# Revit family: VIESSMANN - Vitocal 350-G Pro
name_source: partatom
category: Wyposażenie mechaniczne
revit_build: Autodesk Revit 2017 (Build: 20160720_1515(x64)
units: mm (PartAtom-declared; Revit-internal decimal feet)

## family parameters
Numer OmniClass = 23.75.10.21.17
Oparty na płaszczyźnie roboczej = Nie
Punkt obliczania pomieszczeń = Nie
Tnij formami wycięć po wczytaniu = Nie
Typ części = Normalny
Tytuł OmniClass = Water-Source Heat Pumps
Współdzielony = Nie
Wymiar okrągłego złącza = Użyj średnicy
Zawsze pionowo = Tak

## types (10) — shared parameters
Autor = www.archispace.pl
Czynnik chłodniczy = R134a
Częstotliwość = 50 Hz
Dopuszczalne ciśnienie robocze. Strona niskociśnieniowa = 1.6 MPa
Dopuszczalne ciśnienie robocze. Strona wysokociśnieniowa = 2.6 MPa
Długość strefy serwisowej od przodu = 800 mm  [stored 2.62467 ft]
Klasa efektywności energetycznej. Zastosowanie średniotemperaturowe (W55) = A+
Liczba biegunów = 3
Liczba obiegów chłodniczych = 1
Model = Solankowa pompa ciepła Vitocal 350-G PRO 80kW / Brine-water heat pump Vitocal 350-G PRO 80kW
Napięcie znamionowe = 400 V
Obieg pierwotny. Dop. ciśnienie robocze = 1.0 MPa
Obieg pierwotny. Ochrona przed zamarzaniem/temperatura początku krystalizacji (zalecany czynnik chłodzący Tyfocor) = -16 °C
Obieg pierwotny. Różnica temperatur = 3 °C
Obieg wtórny. Dop. ciśnienie robocze = 1.0 MPa
Obieg wtórny. Maks. temperatura na zasilaniu na wlocie z obiegu pierwotnego B -2°C = 73 °C
Obieg wtórny. Min. temperatura na zasilaniu zasobnika lodu = -10 °C
Obieg wtórny. Różnica temperatur = 5 °C
Opis = Pompy ciepła z napędem elektrycznym do ogrzewania i podgrzewu ciepłej wody użytkowej w jedno- lub dwusystemowych instalacjach grzewczych.
Podłączenie A odsunięcie = 389 mm  [stored 1.27625 ft]
Podłączenie A wysokość = 964 mm  [stored 3.16273 ft]
Podłączenie B odsunięcie = 389 mm  [stored 1.27625 ft]
Podłączenie B wysokość = 504 mm  [stored 1.65354 ft]
Podłączenie C odsunięcie = 106 mm  [stored 0.347769 ft]
Podłączenie C wysokość = 964 mm  [stored 3.16273 ft]
Podłączenie D odsunięcie = 106 mm  [stored 0.347769 ft]
Podłączenie D wysokość = 504 mm  [stored 1.65354 ft]
Podłączenie elektryczne odsunięcie = 697 mm
Podłączenie elektryczne wysokość = 1366 mm
Producent = Viessmann Sp. z o.o.
Rodzaj sprężarki = Tłok
Stopień ochrony = IP20
System rozruchowy = Moduł łagodnego rozruchu
URL = https://www.viessmann-projektant.pl
Viessmann Kolor 1 = Viessmann Kolor 1
Wewnętrzne zabezpieczenie pomp i zaworów (3/N/PE) = C40A
Zasilanie elektryczne (V/ph/Hz) = 3LNPE/400 V/50 Hz

## per-type parameters (varying)
- BW 352.B027: Całkowity maksymalny pobór mocy=31.0 kW; Całkowity prąd rozruchowy=74 A; Cos Phi sprężarki przy maks. mocy w B15/W35=0.63; Dane dotyczące mocy w trybie grzewczym. Zastosowanie niskotemperaturowe (W35). Efektywność energetyczna=147.00%; Dane dotyczące mocy w trybie grzewczym. Zastosowanie niskotemperaturowe (W35). Sezonowy stopień efektywności (SCOP)=3.87; Dane dotyczące mocy w trybie grzewczym. Zastosowanie średniotemperaturowe (W55). Efektywność energetyczna=112.00%; Dane dotyczące mocy w trybie grzewczym. Zastosowanie średniotemperaturowe (W55). Sezonowy stopień efektywności (SCOP)=3.01; Długość całkowita=1848 mm  [stored 6.06299 ft]; Ilość oleju=5.0 L; Klasa efektywności energetycznej. Zastosowanie niskotemperaturowe (W35)=A+; Liczba sprężarek=2; Maks. prąd roboczy=55 A; Maksymalne dopuszczalne zabezpieczenie zasilania przez inwestora=63 A; Masa całkowita (urządzenie podstawowe bez opcjonalnej obudowy)=555.00 kg; Natężenie znamionowe sprężarek (łącznie)=15 A; Obciążenie pozorne=49206 VA; Obieg pierwotny od strony parownika (Victaulic)=2½" (DN 65); Obieg pierwotny od strony zestawu przyłączy (kołnierz)=DN 65/PN 10; Obieg pierwotny. Minimalny przepływ objętościowy=4.8 m³/h; Obieg pierwotny. Opór przepływu przy minimalnym przepływie objętościowym=7.0 kPa; Obieg pierwotny. Opór przepływu przy znamionowym przepływie objętościowym (całkowita strata ciśnienia skraplacza z przyłączami)=12.0 kPa; Obieg pierwotny. Pojemność wymiennika ciepła (solanka)=4.4 L; Obieg pierwotny. Znamionowy przepływ objętościowy (wartość zalecana do projektowania)=6.4 m³/h; Obieg wtórny od strony skraplacza (Victaulic)=2½" (DN 65); Obieg wtórny od strony zestawu przyłączy (kołnierz)=DN 65/PN 10; Obieg wtórny. Minimalny przepływ objętościowy=3.5 m³/h; Obieg wtórny. Opór przepływu przy minimalnym przepływie objętościowym=8.0 kPa; Obieg wtórny. Opór przepływu przy znamionowym przepływie objętościowym (całkowita strata ciśnienia skraplacza z przyłączami)=15.0 kPa; Obieg wtórny. Pojemność wymiennika ciepła (woda)=3.7 L; Obieg wtórny. Znamionowy przepływ objętościowy (wartość zalecana do projektowania)=4.7 m³/h; Odsunięcie strefy serwisowej w szerokości=406 mm; Pobór mocy elektrycznej=6.4 kW; Poziom mocy akustycznej=53 dB(A); Prąd rozruchowy jednej sprężarki=32 A; Stopień efektywności ε (COP)=4.2; Szerokość całkowita=811 mm  [stored 2.66076 ft]; Typ=Vitocal 350-G Pro : BW 352.B027, BW 352.B034, BW 352.B056; Wewnętrzne zabezpieczenie na sprężarkę (3/N/PE)=gG25A; Wielkość napełnienia (wytyczna)=4.20 kg; Współczynnik mocy=0.63; Wydajność chłodnicza=20.8 kW; Wysokość całkowita=1450 mm  [stored 4.75722 ft]; Znamionowa moc grzewcza=27.2 kW; Średnica odejścia 1=65 mm  [stored 0.213255 ft]; Średnica odejścia 2=65 mm  [stored 0.213255 ft]
- BW 352.B034: Całkowity maksymalny pobór mocy=35.0 kW; Całkowity prąd rozruchowy=84 A; Cos Phi sprężarki przy maks. mocy w B15/W35=0.63; Dane dotyczące mocy w trybie grzewczym. Zastosowanie niskotemperaturowe (W35). Efektywność energetyczna=150.00%; Dane dotyczące mocy w trybie grzewczym. Zastosowanie niskotemperaturowe (W35). Sezonowy stopień efektywności (SCOP)=3.96; Dane dotyczące mocy w trybie grzewczym. Zastosowanie średniotemperaturowe (W55). Efektywność energetyczna=115.00%; Dane dotyczące mocy w trybie grzewczym. Zastosowanie średniotemperaturowe (W55). Sezonowy stopień efektywności (SCOP)=3.08; Długość całkowita=1848 mm  [stored 6.06299 ft]; Ilość oleju=6.6 L; Klasa efektywności energetycznej. Zastosowanie niskotemperaturowe (W35)=A++; Liczba sprężarek=2; Maks. prąd roboczy=61 A; Maksymalne dopuszczalne zabezpieczenie zasilania przez inwestora=63 A; Masa całkowita (urządzenie podstawowe bez opcjonalnej obudowy)=672.00 kg; Natężenie znamionowe sprężarek (łącznie)=18 A; Obciążenie pozorne=55556 VA; Obieg pierwotny od strony parownika (Victaulic)=2½" (DN 65); Obieg pierwotny od strony zestawu przyłączy (kołnierz)=DN 65/PN 10; Obieg pierwotny. Minimalny przepływ objętościowy=6.1 m³/h; Obieg pierwotny. Opór przepływu przy minimalnym przepływie objętościowym=7.0 kPa; Obieg pierwotny. Opór przepływu przy znamionowym przepływie objętościowym (całkowita strata ciśnienia skraplacza z przyłączami)=13.0 kPa; Obieg pierwotny. Pojemność wymiennika ciepła (solanka)=5.5 L; Obieg pierwotny. Znamionowy przepływ objętościowy (wartość zalecana do projektowania)=8.2 m³/h; Obieg wtórny od strony skraplacza (Victaulic)=2½" (DN 65); Obieg wtórny od strony zestawu przyłączy (kołnierz)=DN 65/PN 10; Obieg wtórny. Minimalny przepływ objętościowy=4.5 m³/h; Obieg wtórny. Opór przepływu przy minimalnym przepływie objętościowym=8.0 kPa; Obieg wtórny. Opór przepływu przy znamionowym przepływie objętościowym (całkowita strata ciśnienia skraplacza z przyłączami)=15.0 kPa; Obieg wtórny. Pojemność wymiennika ciepła (woda)=4.7 L; Obieg wtórny. Znamionowy przepływ objętościowy (wartość zalecana do projektowania)=5.9 m³/h; Odsunięcie strefy serwisowej w szerokości=406 mm; Pobór mocy elektrycznej=7.9 kW; Poziom mocy akustycznej=54 dB(A); Prąd rozruchowy jednej sprężarki=39 A; Stopień efektywności ε (COP)=4.4; Szerokość całkowita=811 mm  [stored 2.66076 ft]; Typ=Vitocal 350-G Pro : BW 352.B027, BW 352.B034, BW 352.B056; Wewnętrzne zabezpieczenie na sprężarkę (3/N/PE)=gG25A; Wielkość napełnienia (wytyczna)=5.20 kg; Współczynnik mocy=0.63; Wydajność chłodnicza=26.4 kW; Wysokość całkowita=1450 mm  [stored 4.75722 ft]; Znamionowa moc grzewcza=34.3 kW; Średnica odejścia 1=65 mm  [stored 0.213255 ft]; Średnica odejścia 2=65 mm  [stored 0.213255 ft]
- BW 352.B056: Całkowity maksymalny pobór mocy=47.0 kW; Całkowity prąd rozruchowy=120 A; Cos Phi sprężarki przy maks. mocy w B15/W35=0.71; Dane dotyczące mocy w trybie grzewczym. Zastosowanie niskotemperaturowe (W35). Efektywność energetyczna=153.00%; Dane dotyczące mocy w trybie grzewczym. Zastosowanie niskotemperaturowe (W35). Sezonowy stopień efektywności (SCOP)=4.03; Dane dotyczące mocy w trybie grzewczym. Zastosowanie średniotemperaturowe (W55). Efektywność energetyczna=117.00%; Dane dotyczące mocy w trybie grzewczym. Zastosowanie średniotemperaturowe (W55). Sezonowy stopień efektywności (SCOP)=3.12; Długość całkowita=1848 mm  [stored 6.06299 ft]; Ilość oleju=6.6 L; Klasa efektywności energetycznej. Zastosowanie niskotemperaturowe (W35)=A++; Liczba sprężarek=2; Maks. prąd roboczy=82 A; Maksymalne dopuszczalne zabezpieczenie zasilania przez inwestora=100 A; Masa całkowita (urządzenie podstawowe bez opcjonalnej obudowy)=723.00 kg; Natężenie znamionowe sprężarek (łącznie)=29 A; Obciążenie pozorne=66197 VA; Obieg pierwotny od strony parownika (Victaulic)=2½" (DN 65); Obieg pierwotny od strony zestawu przyłączy (kołnierz)=DN 65/PN 10; Obieg pierwotny. Minimalny przepływ objętościowy=10.1 m³/h; Obieg pierwotny. Opór przepływu przy minimalnym przepływie objętościowym=8.0 kPa; Obieg pierwotny. Opór przepływu przy znamionowym przepływie objętościowym (całkowita strata ciśnienia skraplacza z przyłączami)=14.0 kPa; Obieg pierwotny. Pojemność wymiennika ciepła (solanka)=9.4 L; Obieg pierwotny. Znamionowy przepływ objętościowy (wartość zalecana do projektowania)=13.4 m³/h; Obieg wtórny od strony skraplacza (Victaulic)=2½" (DN 65); Obieg wtórny od strony zestawu przyłączy (kołnierz)=DN 65/PN 10; Obieg wtórny. Minimalny przepływ objętościowy=7.3 m³/h; Obieg wtórny. Opór przepływu przy minimalnym przepływie objętościowym=9.0 kPa; Obieg wtórny. Opór przepływu przy znamionowym przepływie objętościowym (całkowita strata ciśnienia skraplacza z przyłączami)=16.0 kPa; Obieg wtórny. Pojemność wymiennika ciepła (woda)=7.4 L; Obieg wtórny. Znamionowy przepływ objętościowy (wartość zalecana do projektowania)=9.7 m³/h; Odsunięcie strefy serwisowej w szerokości=406 mm; Pobór mocy elektrycznej=12.8 kW; Poziom mocy akustycznej=58 dB(A); Prąd rozruchowy jednej sprężarki=65 A; Stopień efektywności ε (COP)=4.4; Szerokość całkowita=811 mm  [stored 2.66076 ft]; Typ=Vitocal 350-G Pro : BW 352.B027, BW 352.B034, BW 352.B056; Wewnętrzne zabezpieczenie na sprężarkę (3/N/PE)=gG40A; Wielkość napełnienia (wytyczna)=5.20 kg; Współczynnik mocy=0.71; Wydajność chłodnicza=43.4 kW; Wysokość całkowita=1450 mm  [stored 4.75722 ft]; Znamionowa moc grzewcza=56.1 kW; Średnica odejścia 1=65 mm  [stored 0.213255 ft]; Średnica odejścia 2=65 mm  [stored 0.213255 ft]
- BW 352.B076: Całkowity maksymalny pobór mocy=56.0 kW; Całkowity prąd rozruchowy=149 A; Cos Phi sprężarki przy maks. mocy w B15/W35=0.71; Dane dotyczące mocy w trybie grzewczym. Zastosowanie niskotemperaturowe (W35). Efektywność energetyczna=154.00%; Dane dotyczące mocy w trybie grzewczym. Zastosowanie niskotemperaturowe (W35). Sezonowy stopień efektywności (SCOP)=4.04; Dane dotyczące mocy w trybie grzewczym. Zastosowanie średniotemperaturowe (W55). Efektywność energetyczna=118.00%; Dane dotyczące mocy w trybie grzewczym. Zastosowanie średniotemperaturowe (W55). Sezonowy stopień efektywności (SCOP)=3.14; Długość całkowita=2153 mm  [stored 7.06365 ft]; Ilość oleju=9.0 L; Klasa efektywności energetycznej. Zastosowanie niskotemperaturowe (W35)=A++; Liczba sprężarek=2; Maks. prąd roboczy=98 A; Maksymalne dopuszczalne zabezpieczenie zasilania przez inwestora=100 A; Masa całkowita (urządzenie podstawowe bez opcjonalnej obudowy)=963.00 kg; Natężenie znamionowe sprężarek (łącznie)=36 A; Obciążenie pozorne=78873 VA; Obieg pierwotny od strony parownika (Victaulic)=2½" (DN 65); Obieg pierwotny od strony zestawu przyłączy (kołnierz)=DN 65/PN 10; Obieg pierwotny. Minimalny przepływ objętościowy=13.6 m³/h; Obieg pierwotny. Opór przepływu przy minimalnym przepływie objętościowym=9.0 kPa; Obieg pierwotny. Opór przepływu przy znamionowym przepływie objętościowym (całkowita strata ciśnienia skraplacza z przyłączami)=17.0 kPa; Obieg pierwotny. Pojemność wymiennika ciepła (solanka)=12.9 L; Obieg pierwotny. Znamionowy przepływ objętościowy (wartość zalecana do projektowania)=18.2 m³/h; Obieg wtórny od strony skraplacza (Victaulic)=2½" (DN 65); Obieg wtórny od strony zestawu przyłączy (kołnierz)=DN 65/PN 10; Obieg wtórny. Minimalny przepływ objętościowy=9.9 m³/h; Obieg wtórny. Opór przepływu przy minimalnym przepływie objętościowym=9.0 kPa; Obieg wtórny. Opór przepływu przy znamionowym przepływie objętościowym (całkowita strata ciśnienia skraplacza z przyłączami)=16.0 kPa; Obieg wtórny. Pojemność wymiennika ciepła (woda)=10.2 L; Obieg wtórny. Znamionowy przepływ objętościowy (wartość zalecana do projektowania)=13.2 m³/h; Odsunięcie strefy serwisowej w szerokości=456 mm; Pobór mocy elektrycznej=17.3 kW; Poziom mocy akustycznej=60 dB(A); Prąd rozruchowy jednej sprężarki=86 A; Stopień efektywności ε (COP)=4.4; Szerokość całkowita=911 mm  [stored 2.98885 ft]; Typ=Vitocal 350-G Pro : BW 352.B076, BW 352.B097, BW 352.B114; Wewnętrzne zabezpieczenie na sprężarkę (3/N/PE)=gG63A; Wielkość napełnienia (wytyczna)=7.50 kg; Współczynnik mocy=0.71; Wydajność chłodnicza=58.8 kW; Wysokość całkowita=1650 mm  [stored 5.41339 ft]; Znamionowa moc grzewcza=76.0 kW; Średnica odejścia 1=65 mm  [stored 0.213255 ft]; Średnica odejścia 2=65 mm  [stored 0.213255 ft]
- BW 352.B097: Całkowity maksymalny pobór mocy=69.0 kW; Całkowity prąd rozruchowy=179 A; Cos Phi sprężarki przy maks. mocy w B15/W35=0.66; Dane dotyczące mocy w trybie grzewczym. Zastosowanie niskotemperaturowe (W35). Efektywność energetyczna=154.00%; Dane dotyczące mocy w trybie grzewczym. Zastosowanie niskotemperaturowe (W35). Sezonowy stopień efektywności (SCOP)=4.06; Dane dotyczące mocy w trybie grzewczym. Zastosowanie średniotemperaturowe (W55). Efektywność energetyczna=118.00%; Dane dotyczące mocy w trybie grzewczym. Zastosowanie średniotemperaturowe (W55). Sezonowy stopień efektywności (SCOP)=3.15; Długość całkowita=2153 mm  [stored 7.06365 ft]; Ilość oleju=10.5 L; Klasa efektywności energetycznej. Zastosowanie niskotemperaturowe (W35)=A++; Liczba sprężarek=2; Maks. prąd roboczy=122 A; Maksymalne dopuszczalne zabezpieczenie zasilania przez inwestora=125 A; Masa całkowita (urządzenie podstawowe bez opcjonalnej obudowy)=1065.00 kg; Natężenie znamionowe sprężarek (łącznie)=54 A; Obciążenie pozorne=104545 VA; Obieg pierwotny od strony parownika (Victaulic)=2½" (DN 65); Obieg pierwotny od strony zestawu przyłączy (kołnierz)=DN 65/PN 10; Obieg pierwotny. Minimalny przepływ objętościowy=17.3 m³/h; Obieg pierwotny. Opór przepływu przy minimalnym przepływie objętościowym=11.0 kPa; Obieg pierwotny. Opór przepływu przy znamionowym przepływie objętościowym (całkowita strata ciśnienia skraplacza z przyłączami)=19.0 kPa; Obieg pierwotny. Pojemność wymiennika ciepła (solanka)=17.7 L; Obieg pierwotny. Znamionowy przepływ objętościowy (wartość zalecana do projektowania)=23.0 m³/h; Obieg wtórny od strony skraplacza (Victaulic)=2½" (DN 65); Obieg wtórny od strony zestawu przyłączy (kołnierz)=DN 65/PN 10; Obieg wtórny. Minimalny przepływ objętościowy=12.6 m³/h; Obieg wtórny. Opór przepływu przy minimalnym przepływie objętościowym=10.0 kPa; Obieg wtórny. Opór przepływu przy znamionowym przepływie objętościowym (całkowita strata ciśnienia skraplacza z przyłączami)=18.0 kPa; Obieg wtórny. Pojemność wymiennika ciepła (woda)=12.7 L; Obieg wtórny. Znamionowy przepływ objętościowy (wartość zalecana do projektowania)=16.8 m³/h; Odsunięcie strefy serwisowej w szerokości=456 mm; Pobór mocy elektrycznej=21.9 kW; Poziom mocy akustycznej=63 dB(A); Prąd rozruchowy jednej sprężarki=104 A; Stopień efektywności ε (COP)=4.4; Szerokość całkowita=911 mm  [stored 2.98885 ft]; Typ=Vitocal 350-G Pro : BW 352.B076, BW 352.B097, BW 352.B114; Wewnętrzne zabezpieczenie na sprężarkę (3/N/PE)=gG63A; Wielkość napełnienia (wytyczna)=10.00 kg; Współczynnik mocy=0.66; Wydajność chłodnicza=74.6 kW; Wysokość całkowita=1650 mm  [stored 5.41339 ft]; Znamionowa moc grzewcza=96.9 kW; Średnica odejścia 1=65 mm  [stored 0.213255 ft]; Średnica odejścia 2=65 mm  [stored 0.213255 ft]
- BW 352.B114: Całkowity maksymalny pobór mocy=78.0 kW; Całkowity prąd rozruchowy=208 A; Cos Phi sprężarki przy maks. mocy w B15/W35=0.7; Dane dotyczące mocy w trybie grzewczym. Zastosowanie niskotemperaturowe (W35). Efektywność energetyczna=153.00%; Dane dotyczące mocy w trybie grzewczym. Zastosowanie niskotemperaturowe (W35). Sezonowy stopień efektywności (SCOP)=4.03; Dane dotyczące mocy w trybie grzewczym. Zastosowanie średniotemperaturowe (W55). Efektywność energetyczna=117.00%; Dane dotyczące mocy w trybie grzewczym. Zastosowanie średniotemperaturowe (W55). Sezonowy stopień efektywności (SCOP)=3.14; Długość całkowita=2153 mm  [stored 7.06365 ft]; Ilość oleju=10.5 L; Klasa efektywności energetycznej. Zastosowanie niskotemperaturowe (W35)=A++; Liczba sprężarek=2; Maks. prąd roboczy=137 A; Maksymalne dopuszczalne zabezpieczenie zasilania przez inwestora=160 A; Masa całkowita (urządzenie podstawowe bez opcjonalnej obudowy)=1113.00 kg; Natężenie znamionowe sprężarek (łącznie)=57 A; Obciążenie pozorne=111429 VA; Obieg pierwotny od strony parownika (Victaulic)=3" (DN 80); Obieg pierwotny od strony zestawu przyłączy (kołnierz)=DN 80/PN 10; Obieg pierwotny. Minimalny przepływ objętościowy=20.5 m³/h; Obieg pierwotny. Opór przepływu przy minimalnym przepływie objętościowym=13.0 kPa; Obieg pierwotny. Opór przepływu przy znamionowym przepływie objętościowym (całkowita strata ciśnienia skraplacza z przyłączami)=23.0 kPa; Obieg pierwotny. Pojemność wymiennika ciepła (solanka)=21.9 L; Obieg pierwotny. Znamionowy przepływ objętościowy (wartość zalecana do projektowania)=27.3 m³/h; Obieg wtórny od strony skraplacza (Victaulic)=3" (DN 80); Obieg wtórny od strony zestawu przyłączy (kołnierz)=DN 80/PN 10; Obieg wtórny. Minimalny przepływ objętościowy=14.8 m³/h; Obieg wtórny. Opór przepływu przy minimalnym przepływie objętościowym=11.0 kPa; Obieg wtórny. Opór przepływu przy znamionowym przepływie objętościowym (całkowita strata ciśnienia skraplacza z przyłączami)=20.0 kPa; Obieg wtórny. Pojemność wymiennika ciepła (woda)=14.9 L; Obieg wtórny. Znamionowy przepływ objętościowy (wartość zalecana do projektowania)=19.8 m³/h; Odsunięcie strefy serwisowej w szerokości=456 mm; Pobór mocy elektrycznej=25.9 kW; Poziom mocy akustycznej=65 dB(A); Prąd rozruchowy jednej sprężarki=126 A; Stopień efektywności ε (COP)=4.4; Szerokość całkowita=911 mm  [stored 2.98885 ft]; Typ=Vitocal 350-G Pro : BW 352.B076, BW 352.B097, BW 352.B114; Wewnętrzne zabezpieczenie na sprężarkę (3/N/PE)=gG63A; Wielkość napełnienia (wytyczna)=12.00 kg; Współczynnik mocy=0.7; Wydajność chłodnicza=88.4 kW; Wysokość całkowita=1650 mm  [stored 5.41339 ft]; Znamionowa moc grzewcza=114.2 kW; Średnica odejścia 1=80 mm  [stored 0.262467 ft]; Średnica odejścia 2=80 mm  [stored 0.262467 ft]
- BW 352.B132: Całkowity maksymalny pobór mocy=89.0 kW; Całkowity prąd rozruchowy=237 A; Cos Phi sprężarki przy maks. mocy w B15/W35=0.66; Dane dotyczące mocy w trybie grzewczym. Zastosowanie niskotemperaturowe (W35). Efektywność energetyczna=150.00%; Dane dotyczące mocy w trybie grzewczym. Zastosowanie niskotemperaturowe (W35). Sezonowy stopień efektywności (SCOP)=3.95; Dane dotyczące mocy w trybie grzewczym. Zastosowanie średniotemperaturowe (W55). Efektywność energetyczna=116.00%; Dane dotyczące mocy w trybie grzewczym. Zastosowanie średniotemperaturowe (W55). Sezonowy stopień efektywności (SCOP)=3.1; Długość całkowita=2153 mm  [stored 7.06365 ft]; Ilość oleju=10.5 L; Klasa efektywności energetycznej. Zastosowanie niskotemperaturowe (W35)=A+; Liczba sprężarek=2; Maks. prąd roboczy=156 A; Maksymalne dopuszczalne zabezpieczenie zasilania przez inwestora=160 A; Masa całkowita (urządzenie podstawowe bez opcjonalnej obudowy)=1209.00 kg; Natężenie znamionowe sprężarek (łącznie)=73 A; Obciążenie pozorne=134848 VA; Obieg pierwotny od strony parownika (Victaulic)=3" (DN 80); Obieg pierwotny od strony zestawu przyłączy (kołnierz)=DN 80/PN 10; Obieg pierwotny. Minimalny przepływ objętościowy=23.5 m³/h; Obieg pierwotny. Opór przepływu przy minimalnym przepływie objętościowym=18.0 kPa; Obieg pierwotny. Opór przepływu przy znamionowym przepływie objętościowym (całkowita strata ciśnienia skraplacza z przyłączami)=32.0 kPa; Obieg pierwotny. Pojemność wymiennika ciepła (solanka)=33.6 L; Obieg pierwotny. Znamionowy przepływ objętościowy (wartość zalecana do projektowania)=31.3 m³/h; Obieg wtórny od strony skraplacza (Victaulic)=3" (DN 80); Obieg wtórny od strony zestawu przyłączy (kołnierz)=DN 80/PN 10; Obieg wtórny. Minimalny przepływ objętościowy=17.1 m³/h; Obieg wtórny. Opór przepływu przy minimalnym przepływie objętościowym=13.0 kPa; Obieg wtórny. Opór przepływu przy znamionowym przepływie objętościowym (całkowita strata ciśnienia skraplacza z przyłączami)=23.0 kPa; Obieg wtórny. Pojemność wymiennika ciepła (woda)=16.7 L; Obieg wtórny. Znamionowy przepływ objętościowy (wartość zalecana do projektowania)=22.9 m³/h; Odsunięcie strefy serwisowej w szerokości=456 mm; Pobór mocy elektrycznej=30.4 kW; Poziom mocy akustycznej=65 dB(A); Prąd rozruchowy jednej sprężarki=144 A; Stopień efektywności ε (COP)=4.3; Szerokość całkowita=911 mm  [stored 2.98885 ft]; Typ=Vitocal 350-G Pro : BW 352.B132, BW 352.B156; Wewnętrzne zabezpieczenie na sprężarkę (3/N/PE)=gG80A; Wielkość napełnienia (wytyczna)=14.00 kg; Współczynnik mocy=0.66; Wydajność chłodnicza=101.5 kW; Wysokość całkowita=1650 mm  [stored 5.41339 ft]; Znamionowa moc grzewcza=131.9 kW; Średnica odejścia 1=80 mm  [stored 0.262467 ft]; Średnica odejścia 2=80 mm  [stored 0.262467 ft]
- BW 352.B156: Całkowity maksymalny pobór mocy=97.0 kW; Całkowity prąd rozruchowy=245 A; Cos Phi sprężarki przy maks. mocy w B15/W35=0.57; Dane dotyczące mocy w trybie grzewczym. Zastosowanie niskotemperaturowe (W35). Efektywność energetyczna=150.00%; Dane dotyczące mocy w trybie grzewczym. Zastosowanie niskotemperaturowe (W35). Sezonowy stopień efektywności (SCOP)=3.95; Dane dotyczące mocy w trybie grzewczym. Zastosowanie średniotemperaturowe (W55). Efektywność energetyczna=116.00%; Dane dotyczące mocy w trybie grzewczym. Zastosowanie średniotemperaturowe (W55). Sezonowy stopień efektywności (SCOP)=3.1; Długość całkowita=2153 mm  [stored 7.06365 ft]; Ilość oleju=10.5 L; Klasa efektywności energetycznej. Zastosowanie niskotemperaturowe (W35)=A+; Liczba sprężarek=2; Maks. prąd roboczy=187 A; Maksymalne dopuszczalne zabezpieczenie zasilania przez inwestora=200 A; Masa całkowita (urządzenie podstawowe bez opcjonalnej obudowy)=1260.00 kg; Natężenie znamionowe sprężarek (łącznie)=102 A; Obciążenie pozorne=170175 VA; Obieg pierwotny od strony parownika (Victaulic)=3" (DN 80); Obieg pierwotny od strony zestawu przyłączy (kołnierz)=DN 80/PN 10; Obieg pierwotny. Minimalny przepływ objętościowy=27.6 m³/h; Obieg pierwotny. Opór przepływu przy minimalnym przepływie objętościowym=19.0 kPa; Obieg pierwotny. Opór przepływu przy znamionowym przepływie objętościowym (całkowita strata ciśnienia skraplacza z przyłączami)=33.0 kPa; Obieg pierwotny. Pojemność wymiennika ciepła (solanka)=39.0 L; Obieg pierwotny. Znamionowy przepływ objętościowy (wartość zalecana do projektowania)=36.8 m³/h; Obieg wtórny od strony skraplacza (Victaulic)=3" (DN 80); Obieg wtórny od strony zestawu przyłączy (kołnierz)=DN 80/PN 10; Obieg wtórny. Minimalny przepływ objętościowy=20.1 m³/h; Obieg wtórny. Opór przepływu przy minimalnym przepływie objętościowym=15.0 kPa; Obieg wtórny. Opór przepływu przy znamionowym przepływie objętościowym (całkowita strata ciśnienia skraplacza z przyłączami)=27.0 kPa; Obieg wtórny. Pojemność wymiennika ciepła (woda)=19.5 L; Obieg wtórny. Znamionowy przepływ objętościowy (wartość zalecana do projektowania)=26.9 m³/h; Odsunięcie strefy serwisowej w szerokości=456 mm; Pobór mocy elektrycznej=36.3 kW; Poziom mocy akustycznej=65 dB(A); Prąd rozruchowy jednej sprężarki=188 A; Stopień efektywności ε (COP)=4.3; Szerokość całkowita=911 mm  [stored 2.98885 ft]; Typ=Vitocal 350-G Pro : BW 352.B132, BW 352.B156; Wewnętrzne zabezpieczenie na sprężarkę (3/N/PE)=gG100A; Wielkość napełnienia (wytyczna)=17.00 kg; Współczynnik mocy=0.57; Wydajność chłodnicza=119.2 kW; Wysokość całkowita=1650 mm  [stored 5.41339 ft]; Znamionowa moc grzewcza=155.0 kW; Średnica odejścia 1=80 mm  [stored 0.262467 ft]; Średnica odejścia 2=80 mm  [stored 0.262467 ft]
- BW 352.B172: Całkowity maksymalny pobór mocy=110.0 kW; Całkowity prąd rozruchowy=262 A; Cos Phi sprężarki przy maks. mocy w B15/W35=0.7; Dane dotyczące mocy w trybie grzewczym. Zastosowanie niskotemperaturowe (W35). Efektywność energetyczna=150.00%; Dane dotyczące mocy w trybie grzewczym. Zastosowanie niskotemperaturowe (W35). Sezonowy stopień efektywności (SCOP)=3.95; Dane dotyczące mocy w trybie grzewczym. Zastosowanie średniotemperaturowe (W55). Efektywność energetyczna=116.00%; Dane dotyczące mocy w trybie grzewczym. Zastosowanie średniotemperaturowe (W55). Sezonowy stopień efektywności (SCOP)=3.1; Długość całkowita=2816 mm  [stored 9.23885 ft]; Ilość oleju=15.8 L; Klasa efektywności energetycznej. Zastosowanie niskotemperaturowe (W35)=A++; Liczba sprężarek=3; Maks. prąd roboczy=191 A; Maksymalne dopuszczalne zabezpieczenie zasilania przez inwestora=200 A; Masa całkowita (urządzenie podstawowe bez opcjonalnej obudowy)=1604.00 kg; Natężenie znamionowe sprężarek (łącznie)=86 A; Obciążenie pozorne=157143 VA; Obieg pierwotny od strony parownika (Victaulic)=3" (DN 80); Obieg pierwotny od strony zestawu przyłączy (kołnierz)=DN 80/PN 10; Obieg pierwotny. Minimalny przepływ objętościowy=30.6 m³/h; Obieg pierwotny. Opór przepływu przy minimalnym przepływie objętościowym=19.0 kPa; Obieg pierwotny. Opór przepływu przy znamionowym przepływie objętościowym (całkowita strata ciśnienia skraplacza z przyłączami)=34.0 kPa; Obieg pierwotny. Pojemność wymiennika ciepła (solanka)=43.2 L; Obieg pierwotny. Znamionowy przepływ objętościowy (wartość zalecana do projektowania)=40.8 m³/h; Obieg wtórny od strony skraplacza (Victaulic)=3" (DN 80); Obieg wtórny od strony zestawu przyłączy (kołnierz)=DN 80/PN 10; Obieg wtórny. Minimalny przepływ objętościowy=22.1 m³/h; Obieg wtórny. Opór przepływu przy minimalnym przepływie objętościowym=16.0 kPa; Obieg wtórny. Opór przepływu przy znamionowym przepływie objętościowym (całkowita strata ciśnienia skraplacza z przyłączami)=28.0 kPa; Obieg wtórny. Pojemność wymiennika ciepła (woda)=22.6 L; Obieg wtórny. Znamionowy przepływ objętościowy (wartość zalecana do projektowania)=29.5 m³/h; Odsunięcie strefy serwisowej w szerokości=456 mm; Pobór mocy elektrycznej=38.4 kW; Poziom mocy akustycznej=65 dB(A); Prąd rozruchowy jednej sprężarki=126 A; Stopień efektywności ε (COP)=4.4; Szerokość całkowita=911 mm  [stored 2.98885 ft]; Typ=Vitocal 350-G Pro : BW 353.B172, BW 353.B198; Wewnętrzne zabezpieczenie na sprężarkę (3/N/PE)=gG63A; Wielkość napełnienia (wytyczna)=19.00 kg; Współczynnik mocy=0.7; Wydajność chłodnicza=132.0 kW; Wysokość całkowita=1650 mm  [stored 5.41339 ft]; Znamionowa moc grzewcza=170.2 kW; Średnica odejścia 1=80 mm  [stored 0.262467 ft]; Średnica odejścia 2=80 mm  [stored 0.262467 ft]
- BW 352.B198: Całkowity maksymalny pobór mocy=125.0 kW; Całkowity prąd rozruchowy=300 A; Cos Phi sprężarki przy maks. mocy w B15/W35=0.66; Dane dotyczące mocy w trybie grzewczym. Zastosowanie niskotemperaturowe (W35). Efektywność energetyczna=149.00%; Dane dotyczące mocy w trybie grzewczym. Zastosowanie niskotemperaturowe (W35). Sezonowy stopień efektywności (SCOP)=3.92; Dane dotyczące mocy w trybie grzewczym. Zastosowanie średniotemperaturowe (W55). Efektywność energetyczna=115.00%; Dane dotyczące mocy w trybie grzewczym. Zastosowanie średniotemperaturowe (W55). Sezonowy stopień efektywności (SCOP)=3.08; Długość całkowita=2816 mm  [stored 9.23885 ft]; Ilość oleju=15.8 L; Klasa efektywności energetycznej. Zastosowanie niskotemperaturowe (W35)=A+; Liczba sprężarek=3; Maks. prąd roboczy=220 A; Maksymalne dopuszczalne zabezpieczenie zasilania przez inwestora=250 A; Masa całkowita (urządzenie podstawowe bez opcjonalnej obudowy)=1678.00 kg; Natężenie znamionowe sprężarek (łącznie)=110 A; Obciążenie pozorne=189394 VA; Obieg pierwotny od strony parownika (Victaulic)=3" (DN 80); Obieg pierwotny od strony zestawu przyłączy (kołnierz)=DN 80/PN 10; Obieg pierwotny. Minimalny przepływ objętościowy=35.5 m³/h; Obieg pierwotny. Opór przepływu przy minimalnym przepływie objętościowym=19.0 kPa; Obieg pierwotny. Opór przepływu przy znamionowym przepływie objętościowym (całkowita strata ciśnienia skraplacza z przyłączami)=35.0 kPa; Obieg pierwotny. Pojemność wymiennika ciepła (solanka)=50.4 L; Obieg pierwotny. Znamionowy przepływ objętościowy (wartość zalecana do projektowania)=47.3 m³/h; Obieg wtórny od strony skraplacza (Victaulic)=3" (DN 80); Obieg wtórny od strony zestawu przyłączy (kołnierz)=DN 80/PN 10; Obieg wtórny. Minimalny przepływ objętościowy=25.6 m³/h; Obieg wtórny. Opór przepływu przy minimalnym przepływie objętościowym=18.0 kPa; Obieg wtórny. Opór przepływu przy znamionowym przepływie objętościowym (całkowita strata ciśnienia skraplacza z przyłączami)=32.0 kPa; Obieg wtórny. Pojemność wymiennika ciepła (woda)=27.9 L; Obieg wtórny. Znamionowy przepływ objętościowy (wartość zalecana do projektowania)=34.1 m³/h; Odsunięcie strefy serwisowej w szerokości=456 mm; Pobór mocy elektrycznej=45.7 kW; Poziom mocy akustycznej=65 dB(A); Prąd rozruchowy jednej sprężarki=144 A; Stopień efektywności ε (COP)=4.3; Szerokość całkowita=911 mm  [stored 2.98885 ft]; Typ=Vitocal 350-G Pro : BW 353.B172, BW 353.B198; Wewnętrzne zabezpieczenie na sprężarkę (3/N/PE)=gG80A; Wielkość napełnienia (wytyczna)=22.00 kg; Współczynnik mocy=0.66; Wydajność chłodnicza=153.3 kW; Wysokość całkowita=1650 mm  [stored 5.41339 ft]; Znamionowa moc grzewcza=197.0 kW; Średnica odejścia 1=80 mm  [stored 0.262467 ft]; Średnica odejścia 2=80 mm  [stored 0.262467 ft]

note: [stored X ft] marks values corroborated as IEEE doubles in the binary element streams (Revit-internal decimal feet)

## geometry (parser evidence)
native form markers: Sweep x3
no freeform markers — native parametric forms only
